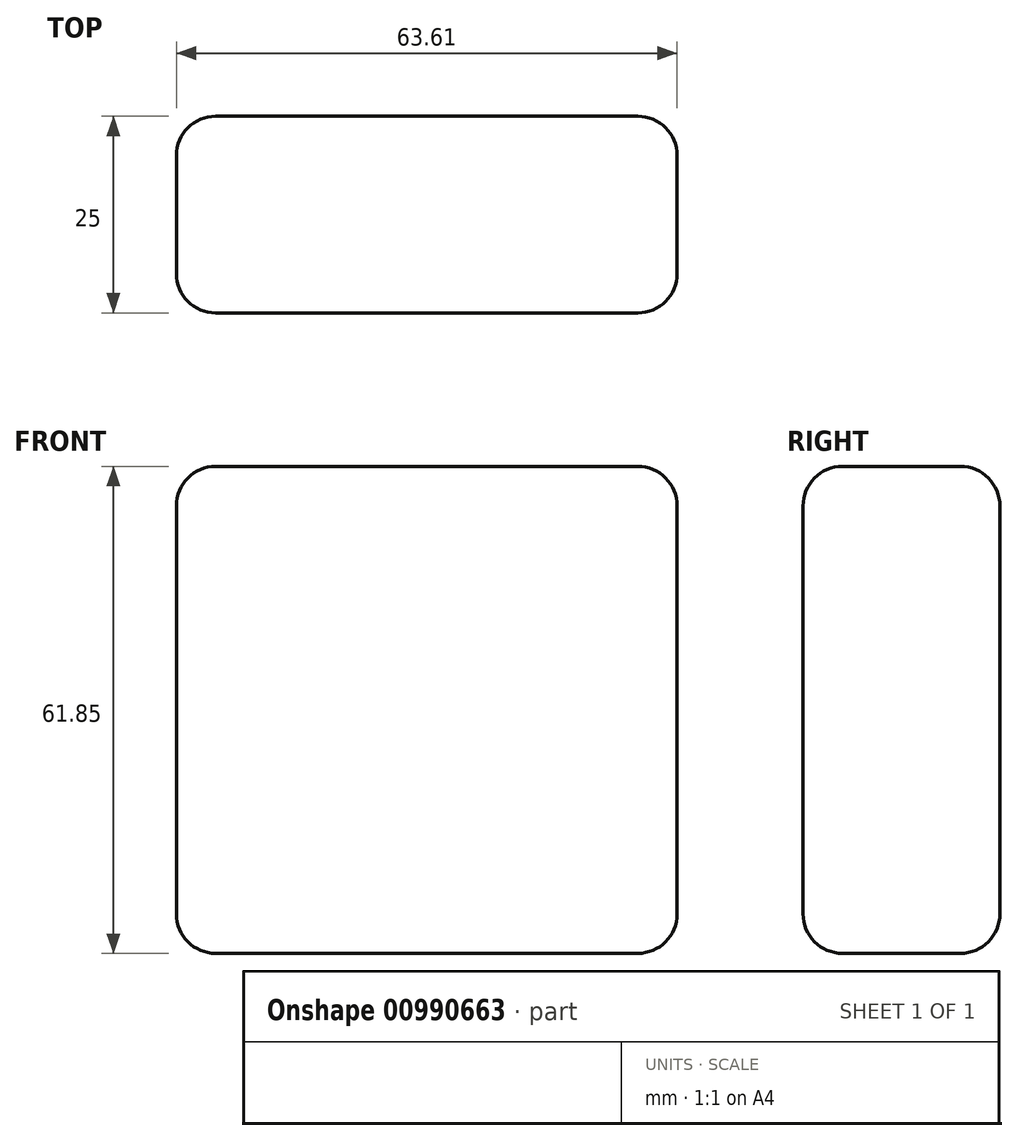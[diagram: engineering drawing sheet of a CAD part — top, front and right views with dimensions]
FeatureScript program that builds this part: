
annotation { "Feature Type Name" : "Feature", "Feature Type Description" : "" }
export const myFeature = defineFeature(function(context is Context, id is Id, definition is map)
    precondition{}
    {
        {
            var Q0;
            Q0=qCreatedBy(makeId("Front.planeOp"),FACE);
            var sketch = newSketch(context, id + "F0", { "sketchPlane" : qUnion([Q0])});
            skLineSegment(sketch, "E0.bottom", {"start": v(-170.88, -80.32) * mm, "end": v(-107.27, -80.32) * mm});
            skLineSegment(sketch, "E0.top", {"start": v(-170.88, -18.47) * mm, "end": v(-107.27, -18.47) * mm});
            skLineSegment(sketch, "E0.left", {"start": v(-170.88, -80.32) * mm, "end": v(-170.88, -18.47) * mm});
            skLineSegment(sketch, "E0.right", {"start": v(-107.27, -80.32) * mm, "end": v(-107.27, -18.47) * mm});
            skPoint(sketch, "E0.middle", {"position": v(-139.07, -49.4) * mm});
            skSolve(sketch);
        }
        {
            var Q0;
            Q0=makeQuery(id+"F0.imprint","IMPRINT",FACE,{"disambiguationData":[TD([[makeQuery(id+"F0.imprint","IMPRINT",EDGE,{"derivedFrom":sQuery(id+"F0.wireOp",EDGE,"E0.bottom")}),1.0]])]});
            extrude(context, id + "F1", {"entities" : qUnion([Q0]), "depth" : 25 * mm, "offsetDistance" : 25 * mm});
        }
        {
            var Q0;
            Q0=makeQuery(id+"F1.opExtrude","CAP_FACE",FACE,{"disambiguationData":[OSD([sQuery(id+"F0.wireOp",EDGE,"E0.bottom"),sQuery(id+"F0.wireOp",EDGE,"E0.top"),sQuery(id+"F0.wireOp",EDGE,"E0.left"),sQuery(id+"F0.wireOp",EDGE,"E0.right")])],"isStart":false});
            var Q1;
            Q1=makeQuery(id+"F1.opExtrude","CAP_FACE",FACE,{"disambiguationData":[OSD([sQuery(id+"F0.wireOp",EDGE,"E0.bottom"),sQuery(id+"F0.wireOp",EDGE,"E0.top"),sQuery(id+"F0.wireOp",EDGE,"E0.left"),sQuery(id+"F0.wireOp",EDGE,"E0.right")])],"isStart":true});
            var Q2;
            Q2=makeQuery(id+"F1.opExtrude","SWEPT_FACE",FACE,{"disambiguationData":[OSD([sQuery(id+"F0.wireOp",EDGE,"E0.top")])]});
            var Q3;
            Q3=makeQuery(id+"F1.opExtrude","SWEPT_FACE",FACE,{"disambiguationData":[OSD([sQuery(id+"F0.wireOp",EDGE,"E0.bottom")])]});
            fillet(context, id + "F2", {"entities" : qUnion([Q0, Q1, Q2, Q3]), "radius" : 5 * mm, "tangentPropagation" : true, "allowEdgeOverflow" : false});
        }
    });
